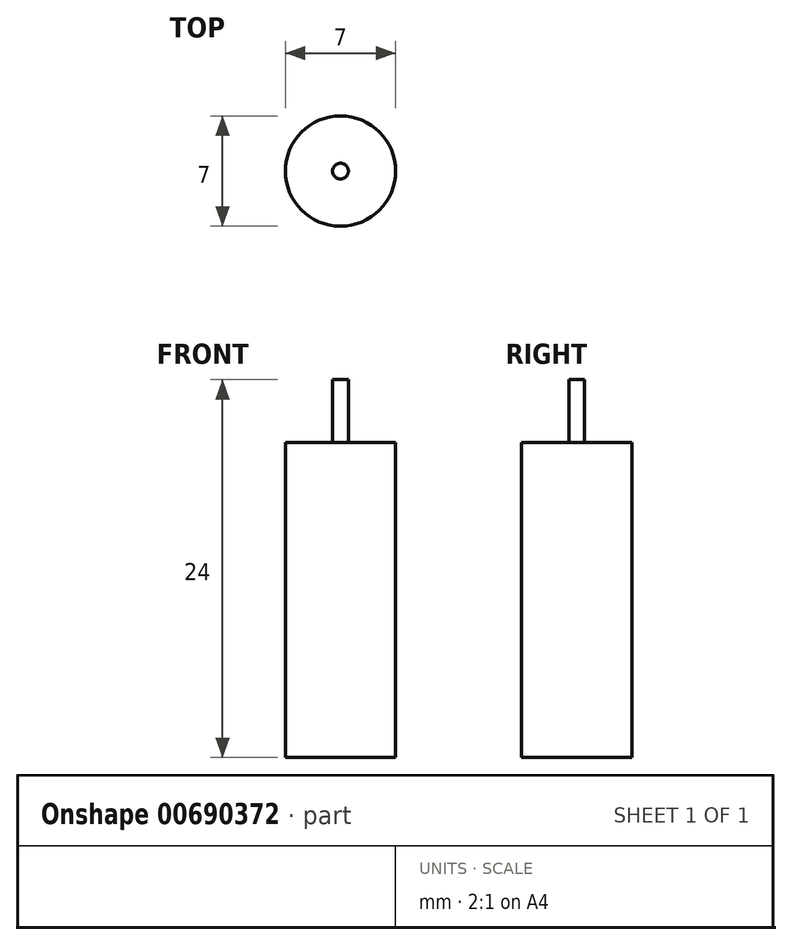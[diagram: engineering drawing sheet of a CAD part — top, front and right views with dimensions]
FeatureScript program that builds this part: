
annotation { "Feature Type Name" : "Feature", "Feature Type Description" : "" }
export const myFeature = defineFeature(function(context is Context, id is Id, definition is map)
    precondition{}
    {
        {
            var Q0;
            Q0=qCreatedBy(makeId("Front.planeOp"),FACE);
            var sketch = newSketch(context, id + "F0", { "sketchPlane" : qUnion([Q0])});
            skLineSegment(sketch, "E0", {"start": v(0, 0) * mm, "end": v(-3.5, 0) * mm});
            skLineSegment(sketch, "E1", {"start": v(-3.5, 0) * mm, "end": v(-3.5, 20) * mm});
            skLineSegment(sketch, "E2", {"start": v(-3.5, 20) * mm, "end": v(-0.5, 20) * mm});
            skLineSegment(sketch, "E3", {"start": v(-0.5, 20) * mm, "end": v(-0.5, 24) * mm});
            skLineSegment(sketch, "E4", {"start": v(-0.5, 24) * mm, "end": v(0, 24) * mm});
            skLineSegment(sketch, "E5", {"start": v(0, 24) * mm, "end": v(0, 0) * mm});
            skSolve(sketch);
        }
        {
            var Q0;
            Q0=makeQuery(id+"F0.imprint","IMPRINT",FACE,{"disambiguationData":[TD([[makeQuery(id+"F0.imprint","IMPRINT",EDGE,{"derivedFrom":sQuery(id+"F0.wireOp",EDGE,"E0")}),-1.0]])]});
            var Q1;
            Q1=sQuery(id+"F0.wireOp",EDGE,"E5");
            revolve(context, id + "F1", {"entities" : qUnion([Q0]), "axis" : qUnion([Q1]), "revolveType" : RevolveType.FULL});
        }
    });
